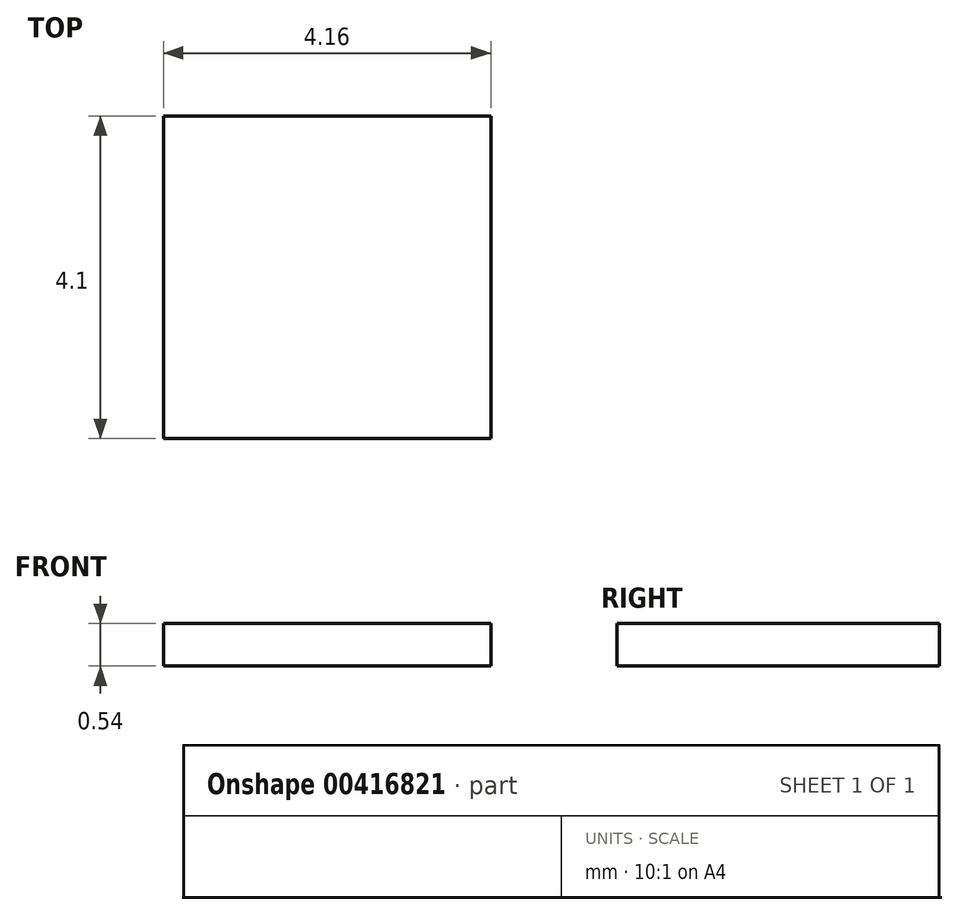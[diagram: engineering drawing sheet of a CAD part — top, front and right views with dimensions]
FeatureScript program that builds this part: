
annotation { "Feature Type Name" : "Feature", "Feature Type Description" : "" }
export const myFeature = defineFeature(function(context is Context, id is Id, definition is map)
    precondition{}
    {
        {
            var Q0;
            Q0=qCreatedBy(makeId("Top.planeOp"),FACE);
            var sketch = newSketch(context, id + "F0", { "sketchPlane" : qUnion([Q0])});
            skLineSegment(sketch, "E0.bottom", {"start": v(0, 0) * mm, "end": v(4.16, 0) * mm});
            skLineSegment(sketch, "E0.top", {"start": v(0, 4.1) * mm, "end": v(4.16, 4.1) * mm});
            skLineSegment(sketch, "E0.left", {"start": v(0, 0) * mm, "end": v(0, 4.1) * mm});
            skLineSegment(sketch, "E0.right", {"start": v(4.16, 0) * mm, "end": v(4.16, 4.1) * mm});
            skSolve(sketch);
        }
        {
            var Q0;
            Q0 = qSketchRegion(id + "F0", true);
            extrude(context, id + "F1", {"entities" : qUnion([Q0]), "depth" : .54 * mm, "offsetDistance" : 25.4 * mm});
        }
    });
